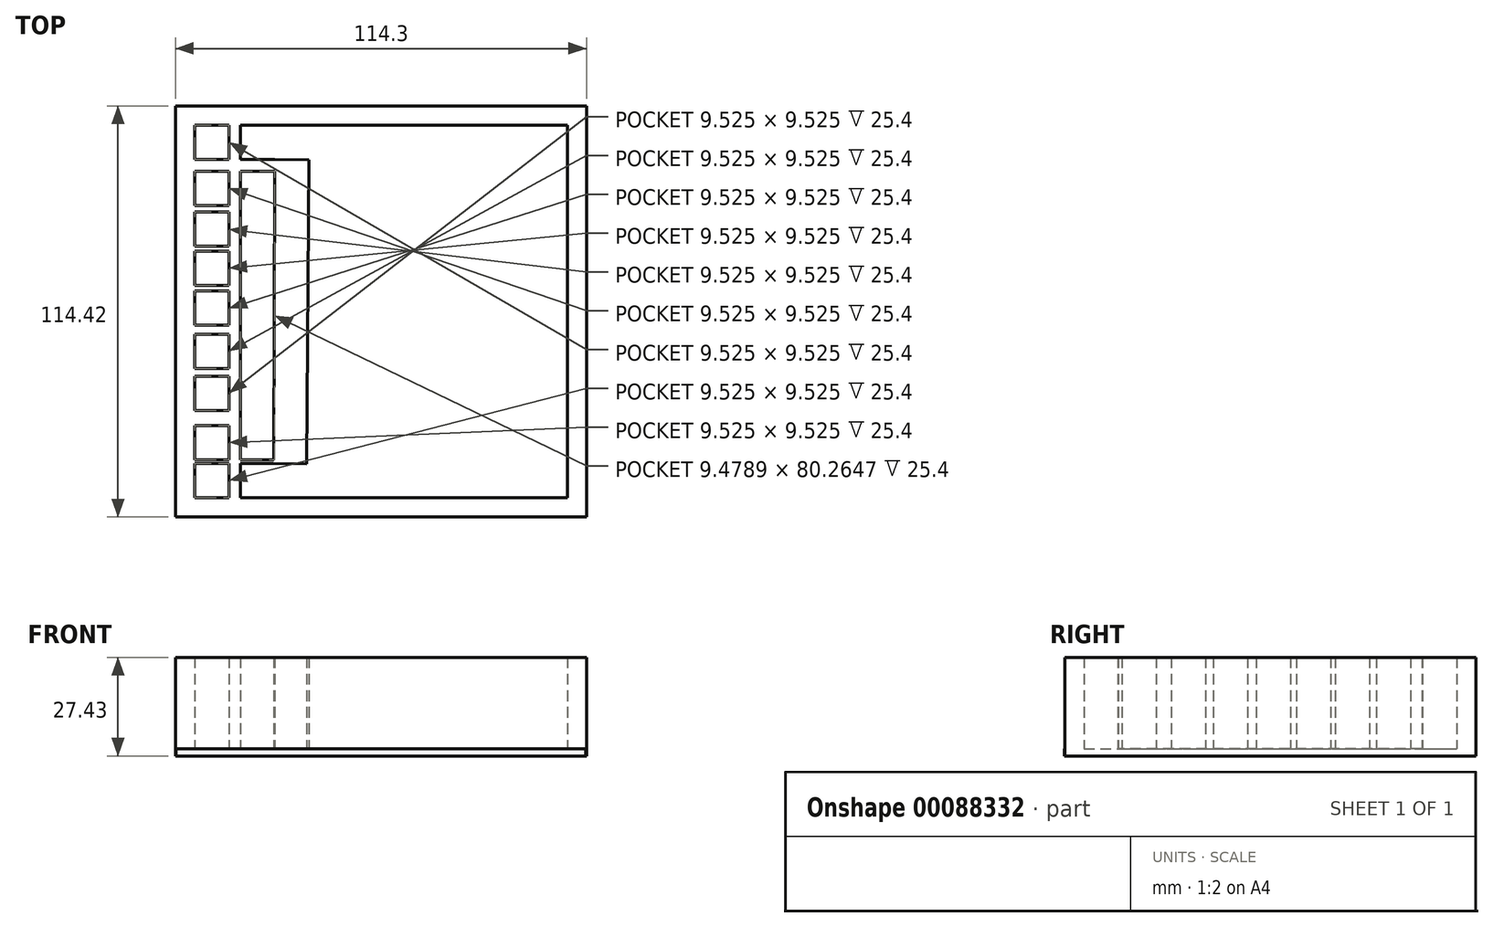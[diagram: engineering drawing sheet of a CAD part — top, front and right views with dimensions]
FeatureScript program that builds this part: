
annotation { "Feature Type Name" : "Feature", "Feature Type Description" : "" }
export const myFeature = defineFeature(function(context is Context, id is Id, definition is map)
    precondition{}
    {
        {
            var Q0;
            Q0=qCreatedBy(makeId("Top.planeOp"),FACE);
            var sketch = newSketch(context, id + "F0", { "sketchPlane" : qUnion([Q0])});
            skLineSegment(sketch, "E0.bottom", {"start": v(57.15, 57.15) * mm, "end": v(-57.15, 57.15) * mm});
            skLineSegment(sketch, "E0.top", {"start": v(57.15, -57.15) * mm, "end": v(-57.15, -57.15) * mm});
            skLineSegment(sketch, "E0.left", {"start": v(57.15, 57.15) * mm, "end": v(57.15, -57.15) * mm});
            skLineSegment(sketch, "E0.right", {"start": v(-57.15, 57.15) * mm, "end": v(-57.15, -57.15) * mm});
            skPoint(sketch, "E0.middle", {"position": v(0, 0) * mm});
            skLineSegment(sketch, "E1.bottom", {"start": v(51.82, -51.82) * mm, "end": v(-51.82, -51.82) * mm});
            skLineSegment(sketch, "E1.top", {"start": v(51.82, 51.82) * mm, "end": v(-51.82, 51.82) * mm});
            skLineSegment(sketch, "E1.left", {"start": v(51.82, -51.82) * mm, "end": v(51.82, 51.82) * mm});
            skLineSegment(sketch, "E1.right", {"start": v(-51.82, -51.82) * mm, "end": v(-51.82, 51.82) * mm});
            skSolve(sketch);
        }
        {
            var Q0;
            Q0 = qSketchRegion(id + "F0", true);
            extrude(context, id + "F1", {"entities" : qUnion([Q0]), "depth" : 27.43 * mm});
        }
        {
            var Q0;
            Q0=qCreatedBy(makeId("Top.planeOp"),FACE);
            var sketch = newSketch(context, id + "F2", { "sketchPlane" : qUnion([Q0])});
            skLineSegment(sketch, "E2.bottom", {"start": v(56.98, -57.2) * mm, "end": v(-56.98, -57.2) * mm});
            skLineSegment(sketch, "E2.top", {"start": v(56.98, 57.2) * mm, "end": v(-56.98, 57.2) * mm});
            skLineSegment(sketch, "E2.left", {"start": v(56.98, -57.2) * mm, "end": v(56.98, 57.2) * mm});
            skLineSegment(sketch, "E2.right", {"start": v(-56.98, -57.2) * mm, "end": v(-56.98, 57.2) * mm});
            skPoint(sketch, "E2.middle", {"position": v(0, 0) * mm});
            skSolve(sketch);
        }
        {
            var Q0;
            Q0 = qSketchRegion(id + "F2", true);
            extrude(context, id + "F3", {"entities" : qUnion([Q0]), "operationType" : NewBodyOperationType.ADD, "depth" : 2.03 * mm});
        }
        {
            var Q0;
            Q0=makeQuery(id+"F3.boolean.opBoolean","SPLIT",FACE,{"disambiguationData":[TD([makeQuery(id+"F1.opExtrude","SWEPT_FACE",FACE,{"disambiguationData":[OSD([sQuery(id+"F0.wireOp",EDGE,"E1.bottom")])]})])],"derivedFrom":makeQuery(id+"F3.opExtrude","CAP_FACE",FACE,{"disambiguationData":[OSD([sQuery(id+"F2.wireOp",EDGE,"E2.bottom"),sQuery(id+"F2.wireOp",EDGE,"E2.top"),sQuery(id+"F2.wireOp",EDGE,"E2.left"),sQuery(id+"F2.wireOp",EDGE,"E2.right")])],"isStart":false})});
            var sketch = newSketch(context, id + "F4", { "sketchPlane" : qUnion([Q0])});
            skLineSegment(sketch, "E3.bottom", {"start": v(-42.3, 51.82) * mm, "end": v(-39.08, 51.82) * mm});
            skLineSegment(sketch, "E3.top", {"start": v(-42.3, -51.82) * mm, "end": v(-39.08, -51.82) * mm});
            skLineSegment(sketch, "E3.left", {"start": v(-42.3, 51.82) * mm, "end": v(-42.3, -51.82) * mm});
            skLineSegment(sketch, "E3.right", {"start": v(-39.08, 51.82) * mm, "end": v(-39.08, -51.82) * mm});
            skLineSegment(sketch, "E4.bottom", {"start": v(-42.3, -41.22) * mm, "end": v(-51.82, -41.22) * mm});
            skLineSegment(sketch, "E4.top", {"start": v(-42.3, -42.3) * mm, "end": v(-51.82, -42.3) * mm});
            skLineSegment(sketch, "E4.left", {"start": v(-42.3, -41.22) * mm, "end": v(-42.3, -42.3) * mm});
            skLineSegment(sketch, "E4.right", {"start": v(-51.82, -41.22) * mm, "end": v(-51.82, -42.3) * mm});
            skLineSegment(sketch, "E5.bottom", {"start": v(-51.82, -31.7) * mm, "end": v(-42.3, -31.7) * mm});
            skLineSegment(sketch, "E5.top", {"start": v(-51.82, -27.53) * mm, "end": v(-42.3, -27.53) * mm});
            skLineSegment(sketch, "E5.left", {"start": v(-51.82, -31.7) * mm, "end": v(-51.82, -27.53) * mm});
            skLineSegment(sketch, "E5.right", {"start": v(-42.3, -31.7) * mm, "end": v(-42.3, -27.53) * mm});
            skLineSegment(sketch, "E6.bottom", {"start": v(-51.82, -18) * mm, "end": v(-42.3, -18) * mm});
            skLineSegment(sketch, "E6.top", {"start": v(-51.82, -15.83) * mm, "end": v(-42.3, -15.83) * mm});
            skLineSegment(sketch, "E6.left", {"start": v(-51.82, -18) * mm, "end": v(-51.82, -15.83) * mm});
            skLineSegment(sketch, "E6.right", {"start": v(-42.3, -18) * mm, "end": v(-42.3, -15.83) * mm});
            skLineSegment(sketch, "E7.bottom", {"start": v(-51.82, -6.3) * mm, "end": v(-42.3, -6.3) * mm});
            skLineSegment(sketch, "E7.top", {"start": v(-51.82, -3.85) * mm, "end": v(-42.3, -3.85) * mm});
            skLineSegment(sketch, "E7.left", {"start": v(-51.82, -6.3) * mm, "end": v(-51.82, -3.85) * mm});
            skLineSegment(sketch, "E7.right", {"start": v(-42.3, -6.3) * mm, "end": v(-42.3, -3.85) * mm});
            skLineSegment(sketch, "E8.bottom", {"start": v(-51.82, 5.67) * mm, "end": v(-42.3, 5.67) * mm});
            skLineSegment(sketch, "E8.top", {"start": v(-51.82, 7.27) * mm, "end": v(-42.3, 7.27) * mm});
            skLineSegment(sketch, "E8.left", {"start": v(-51.82, 5.67) * mm, "end": v(-51.82, 7.27) * mm});
            skLineSegment(sketch, "E8.right", {"start": v(-42.3, 5.67) * mm, "end": v(-42.3, 7.27) * mm});
            skLineSegment(sketch, "E9.bottom", {"start": v(-51.82, 16.8) * mm, "end": v(-42.3, 16.8) * mm});
            skLineSegment(sketch, "E9.top", {"start": v(-51.82, 18.11) * mm, "end": v(-42.3, 18.11) * mm});
            skLineSegment(sketch, "E9.left", {"start": v(-51.82, 16.8) * mm, "end": v(-51.82, 18.11) * mm});
            skLineSegment(sketch, "E9.right", {"start": v(-42.3, 16.8) * mm, "end": v(-42.3, 18.11) * mm});
            skLineSegment(sketch, "E10.bottom", {"start": v(-51.82, 27.64) * mm, "end": v(-42.3, 27.64) * mm});
            skLineSegment(sketch, "E10.top", {"start": v(-51.82, 29.52) * mm, "end": v(-42.3, 29.52) * mm});
            skLineSegment(sketch, "E10.left", {"start": v(-51.82, 27.64) * mm, "end": v(-51.82, 29.52) * mm});
            skLineSegment(sketch, "E10.right", {"start": v(-42.3, 27.64) * mm, "end": v(-42.3, 29.52) * mm});
            skLineSegment(sketch, "E11.bottom", {"start": v(-51.82, 39.05) * mm, "end": v(-42.3, 39.05) * mm});
            skLineSegment(sketch, "E11.top", {"start": v(-51.82, 42.3) * mm, "end": v(-42.3, 42.3) * mm});
            skLineSegment(sketch, "E11.left", {"start": v(-51.82, 39.05) * mm, "end": v(-51.82, 42.3) * mm});
            skLineSegment(sketch, "E11.right", {"start": v(-42.3, 39.05) * mm, "end": v(-42.3, 42.3) * mm});
            skLineSegment(sketch, "E12", {"start": v(-40.68, 51.82) * mm, "end": v(-40.68, -51.82) * mm, "construction": true});
            skLineSegment(sketch, "E13.MirrorCS", {"start": v(-39.08, -42.3) * mm, "end": v(-29.55, -42.3) * mm});
            skLineSegment(sketch, "E14.MirrorCS", {"start": v(-39.08, -41.22) * mm, "end": v(-29.55, -41.22) * mm});
            skLineSegment(sketch, "E15.MirrorCS", {"start": v(-29.55, -31.7) * mm, "end": v(-39.08, -31.7) * mm});
            skLineSegment(sketch, "E16.MirrorCS", {"start": v(-29.55, -27.53) * mm, "end": v(-39.08, -27.53) * mm});
            skLineSegment(sketch, "E17.MirrorCS", {"start": v(-29.55, -18) * mm, "end": v(-39.08, -18) * mm});
            skLineSegment(sketch, "E18.MirrorCS", {"start": v(-29.55, -6.3) * mm, "end": v(-39.08, -6.3) * mm});
            skLineSegment(sketch, "E19.MirrorCS", {"start": v(-29.55, -3.85) * mm, "end": v(-39.08, -3.85) * mm});
            skLineSegment(sketch, "E20.MirrorCS", {"start": v(-29.55, -15.83) * mm, "end": v(-39.08, -15.83) * mm});
            skLineSegment(sketch, "E21.MirrorCS", {"start": v(-29.55, 5.67) * mm, "end": v(-39.08, 5.67) * mm});
            skLineSegment(sketch, "E22.MirrorCS", {"start": v(-29.55, 7.27) * mm, "end": v(-39.08, 7.27) * mm});
            skLineSegment(sketch, "E23.MirrorCS", {"start": v(-29.55, 16.8) * mm, "end": v(-39.08, 16.8) * mm});
            skLineSegment(sketch, "E24.MirrorCS", {"start": v(-29.55, 18.11) * mm, "end": v(-39.08, 18.11) * mm});
            skLineSegment(sketch, "E25.MirrorCS", {"start": v(-29.55, 27.64) * mm, "end": v(-39.08, 27.64) * mm});
            skLineSegment(sketch, "E26.MirrorCS", {"start": v(-29.55, 29.52) * mm, "end": v(-39.08, 29.52) * mm});
            skLineSegment(sketch, "E27.MirrorCS", {"start": v(-29.55, 39.05) * mm, "end": v(-39.08, 39.05) * mm});
            skLineSegment(sketch, "E28.MirrorCS", {"start": v(-29.55, 42.3) * mm, "end": v(-39.08, 42.3) * mm});
            skLineSegment(sketch, "E29", {"start": v(-29.93, -51.82) * mm, "end": v(-29.55, 51.82) * mm, "construction": true});
            skLineSegment(sketch, "E30.MirrorCS", {"start": v(-20.7, -41.28) * mm, "end": v(-30.23, -41.21) * mm});
            skLineSegment(sketch, "E31.MirrorCS", {"start": v(-20.7, -42.36) * mm, "end": v(-30.23, -42.29) * mm});
            skLineSegment(sketch, "E32.MirrorCS", {"start": v(-30.16, -31.7) * mm, "end": v(-20.63, -31.76) * mm});
            skLineSegment(sketch, "E33.MirrorCS", {"start": v(-30.13, -27.52) * mm, "end": v(-20.6, -27.6) * mm});
            skLineSegment(sketch, "E34.MirrorCS", {"start": v(-30.06, -18) * mm, "end": v(-20.53, -18.07) * mm});
            skLineSegment(sketch, "E35.MirrorCS", {"start": v(-30.04, -15.83) * mm, "end": v(-20.52, -15.9) * mm});
            skLineSegment(sketch, "E36.MirrorCS", {"start": v(-29.97, -6.3) * mm, "end": v(-20.45, -6.37) * mm});
            skLineSegment(sketch, "E37.MirrorCS", {"start": v(-29.96, -3.85) * mm, "end": v(-20.43, -3.92) * mm});
            skLineSegment(sketch, "E38.MirrorCS", {"start": v(-29.89, 5.68) * mm, "end": v(-20.36, 5.6) * mm});
            skLineSegment(sketch, "E39.MirrorCS", {"start": v(-29.87, 7.27) * mm, "end": v(-20.35, 7.2) * mm});
            skLineSegment(sketch, "E40.MirrorCS", {"start": v(-29.8, 16.8) * mm, "end": v(-20.28, 16.73) * mm});
            skLineSegment(sketch, "E41.MirrorCS", {"start": v(-29.8, 18.11) * mm, "end": v(-20.27, 18.04) * mm});
            skLineSegment(sketch, "E42.MirrorCS", {"start": v(-29.73, 27.64) * mm, "end": v(-20.2, 27.57) * mm});
            skLineSegment(sketch, "E43.MirrorCS", {"start": v(-29.71, 29.52) * mm, "end": v(-20.19, 29.45) * mm});
            skLineSegment(sketch, "E44.MirrorCS", {"start": v(-29.65, 39.05) * mm, "end": v(-20.12, 38.98) * mm});
            skLineSegment(sketch, "E45.MirrorCS", {"start": v(-29.62, 42.3) * mm, "end": v(-20.1, 42.22) * mm});
            skLineSegment(sketch, "E46.MirrorCS", {"start": v(-20.03, 51.75) * mm, "end": v(-20.78, -51.88) * mm});
            skLineSegment(sketch, "E47.MirrorCS", {"start": v(-7.45, 29.36) * mm, "end": v(-16.98, 29.43) * mm});
            skLineSegment(sketch, "E48.MirrorCS", {"start": v(-7.47, 27.48) * mm, "end": v(-16.99, 27.55) * mm});
            skLineSegment(sketch, "E49.MirrorCS", {"start": v(-7.38, 38.89) * mm, "end": v(-16.9, 38.96) * mm});
            skLineSegment(sketch, "E50.MirrorCS", {"start": v(-7.54, 16.64) * mm, "end": v(-17.07, 16.7) * mm});
            skLineSegment(sketch, "E51.MirrorCS", {"start": v(-7.53, 17.95) * mm, "end": v(-17.06, 18.02) * mm});
            skLineSegment(sketch, "E52.MirrorCS", {"start": v(-7.62, 5.51) * mm, "end": v(-17.15, 5.58) * mm});
            skLineSegment(sketch, "E53.MirrorCS", {"start": v(-7.61, 7.11) * mm, "end": v(-17.14, 7.18) * mm});
            skLineSegment(sketch, "E54.MirrorCS", {"start": v(-7.7, -4.01) * mm, "end": v(-17.22, -3.94) * mm});
            skLineSegment(sketch, "E55.MirrorCS", {"start": v(-7.71, -6.47) * mm, "end": v(-17.24, -6.4) * mm});
            skLineSegment(sketch, "E56.MirrorCS", {"start": v(-7.8, -18.16) * mm, "end": v(-17.32, -18.1) * mm});
            skLineSegment(sketch, "E57.MirrorCS", {"start": v(-7.78, -15.99) * mm, "end": v(-17.3, -15.92) * mm});
            skLineSegment(sketch, "E58.MirrorCS", {"start": v(-16.82, 51.72) * mm, "end": v(-17.56, -51.9) * mm});
            skLineSegment(sketch, "E59.MirrorCS", {"start": v(-7.86, -27.68) * mm, "end": v(-17.39, -27.62) * mm});
            skLineSegment(sketch, "E60.MirrorCS", {"start": v(-7.9, -31.85) * mm, "end": v(-17.42, -31.78) * mm});
            skLineSegment(sketch, "E61.MirrorCS", {"start": v(-17.49, -41.3) * mm, "end": v(-7.96, -41.38) * mm});
            skLineSegment(sketch, "E62.MirrorCS", {"start": v(-17.5, -42.38) * mm, "end": v(-7.97, -42.45) * mm});
            skLineSegment(sketch, "E63", {"start": v(-29.93, -51.82) * mm, "end": v(-29.55, 51.82) * mm});
            skSolve(sketch);
        }
        {
            var Q0;
            Q0 = qSketchRegion(id + "F4", true);
            extrude(context, id + "F5", {"entities" : qUnion([Q0]), "operationType" : NewBodyOperationType.ADD, "depth" : 25.4 * mm});
        }
        {
            var Q0;
            Q0 = qSketchRegion(id + "F4", true);
            extrude(context, id + "F6", {"entities" : qUnion([Q0]), "operationType" : NewBodyOperationType.ADD, "depth" : 25.4 * mm});
        }
    });
